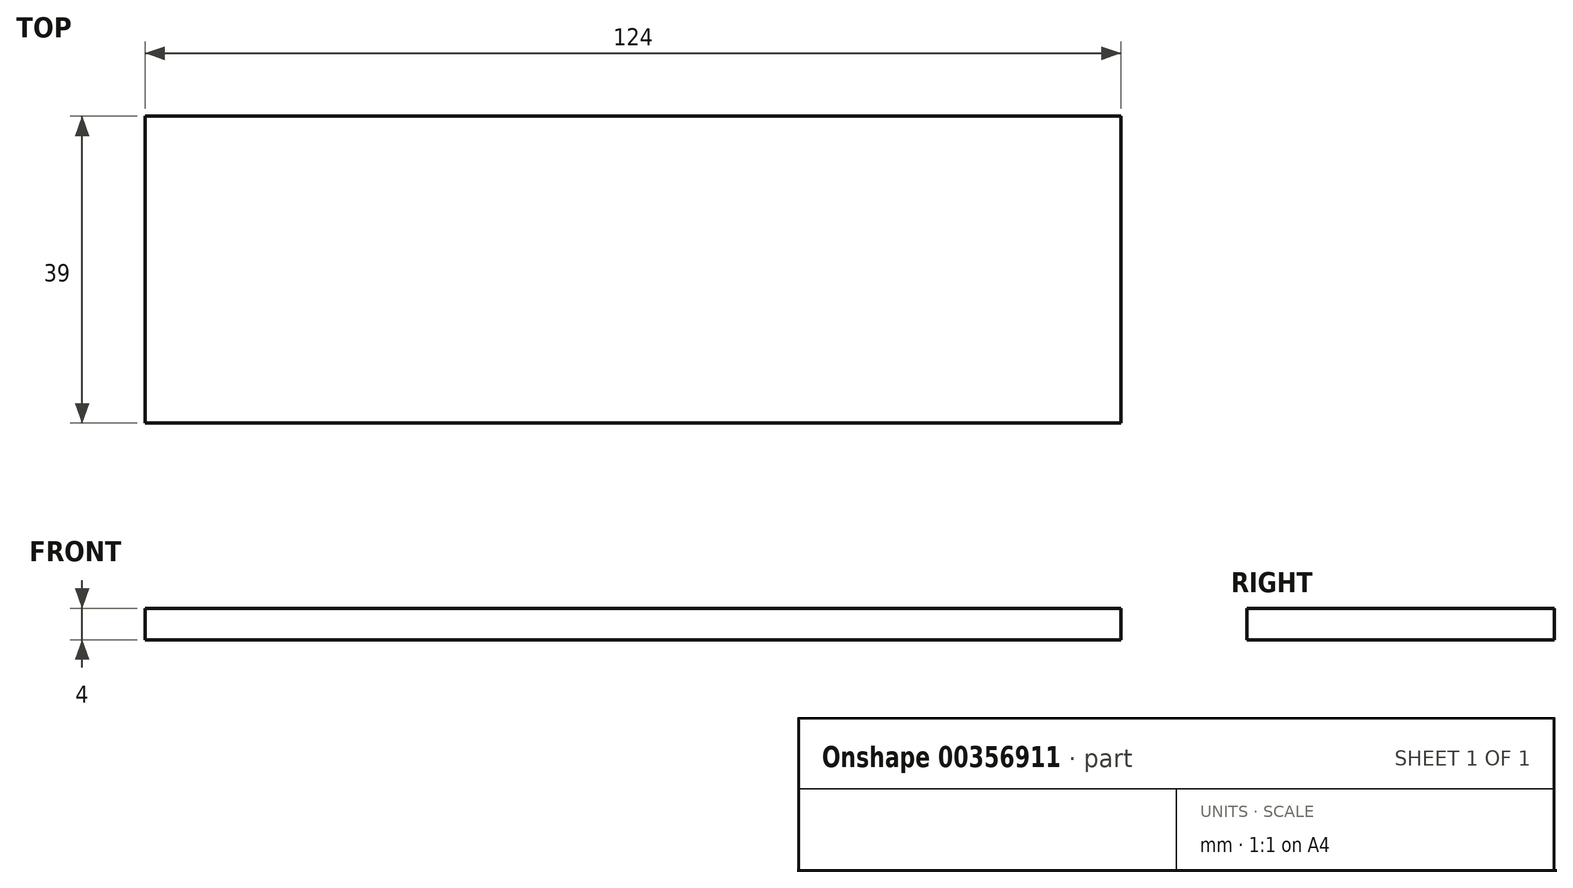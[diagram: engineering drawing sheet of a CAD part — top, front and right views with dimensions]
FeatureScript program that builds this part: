
annotation { "Feature Type Name" : "Feature", "Feature Type Description" : "" }
export const myFeature = defineFeature(function(context is Context, id is Id, definition is map)
    precondition{}
    {
        {
            var Q0;
            Q0=qCreatedBy(makeId("Top.planeOp"),FACE);
            var sketch = newSketch(context, id + "F0", { "sketchPlane" : qUnion([Q0])});
            skLineSegment(sketch, "E0.bottom", {"start": v(-62, 19.5) * mm, "end": v(62, 19.5) * mm});
            skLineSegment(sketch, "E0.top", {"start": v(-62, -19.5) * mm, "end": v(62, -19.5) * mm});
            skLineSegment(sketch, "E0.left", {"start": v(-62, 19.5) * mm, "end": v(-62, -19.5) * mm});
            skLineSegment(sketch, "E0.right", {"start": v(62, 19.5) * mm, "end": v(62, -19.5) * mm});
            skPoint(sketch, "E0.middle", {"position": v(0, 0) * mm});
            skSolve(sketch);
        }
        {
            var Q0;
            Q0=qSketchRegion(id+"F0",true);
            extrude(context, id + "F1", {"entities" : qUnion([Q0]), "depth" : 4 * mm});
        }
    });
